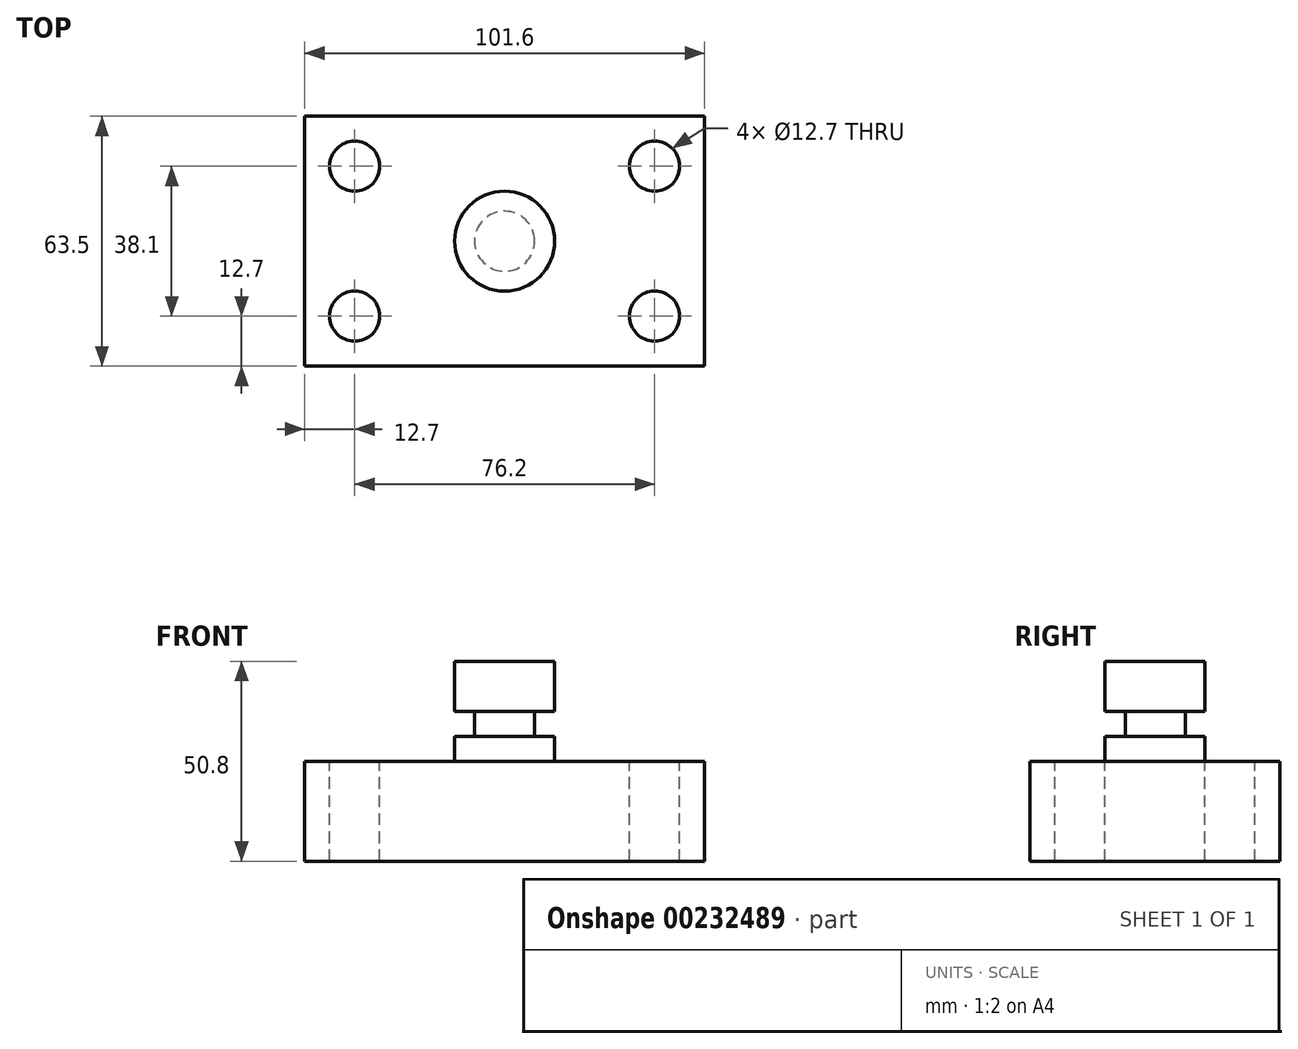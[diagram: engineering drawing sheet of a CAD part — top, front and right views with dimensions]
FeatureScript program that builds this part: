
annotation { "Feature Type Name" : "Feature", "Feature Type Description" : "" }
export const myFeature = defineFeature(function(context is Context, id is Id, definition is map)
    precondition{}
    {
        {
            var Q0;
            Q0=qCreatedBy(makeId("Top.planeOp"),FACE);
            var sketch = newSketch(context, id + "F0", { "sketchPlane" : qUnion([Q0])});
            skLineSegment(sketch, "E0.bottom", {"start": v(-50.8, 31.75) * mm, "end": v(50.8, 31.75) * mm});
            skLineSegment(sketch, "E0.top", {"start": v(-50.8, -31.75) * mm, "end": v(50.8, -31.75) * mm});
            skLineSegment(sketch, "E0.left", {"start": v(-50.8, 31.75) * mm, "end": v(-50.8, -31.75) * mm});
            skLineSegment(sketch, "E0.right", {"start": v(50.8, 31.75) * mm, "end": v(50.8, -31.75) * mm});
            skPoint(sketch, "E0.middle", {"position": v(0, 0) * mm});
            skSolve(sketch);
        }
        {
            var Q0;
            Q0 = qSketchRegion(id + "F0", true);
            extrude(context, id + "F1", {"entities" : qUnion([Q0]), "depth" : 25.4 * mm});
        }
        {
            var Q0;
            Q0=makeQuery(id+"F1.opExtrude","CAP_FACE",FACE,{"disambiguationData":[OSD([sQuery(id+"F0.wireOp",EDGE,"E0.bottom"),sQuery(id+"F0.wireOp",EDGE,"E0.top"),sQuery(id+"F0.wireOp",EDGE,"E0.left"),sQuery(id+"F0.wireOp",EDGE,"E0.right")])],"isStart":false});
            var sketch = newSketch(context, id + "F2", { "sketchPlane" : qUnion([Q0])});
            skCircle(sketch, "E1", {"center": v(38.1, 19.05) * mm, "radius": 6.35 * mm});
            skCircle(sketch, "E2", {"center": v(-38.1, 19.05) * mm, "radius": 6.35 * mm});
            skCircle(sketch, "E3", {"center": v(-38.1, -19.05) * mm, "radius": 6.35 * mm});
            skCircle(sketch, "E4", {"center": v(38.1, -19.05) * mm, "radius": 6.35 * mm});
            skSolve(sketch);
        }
        {
            var Q0;
            Q0=makeQuery(id+"F2.imprint","IMPRINT",FACE,{"disambiguationData":[TD([[makeQuery(id+"F2.imprint","IMPRINT",EDGE,{"derivedFrom":sQuery(id+"F2.wireOp",EDGE,"E1")}),1.0]])]});
            var Q1;
            Q1=makeQuery(id+"F2.imprint","IMPRINT",FACE,{"disambiguationData":[TD([[makeQuery(id+"F2.imprint","IMPRINT",EDGE,{"derivedFrom":sQuery(id+"F2.wireOp",EDGE,"E3")}),1.0]])]});
            var Q2;
            Q2=makeQuery(id+"F2.imprint","IMPRINT",FACE,{"disambiguationData":[TD([[makeQuery(id+"F2.imprint","IMPRINT",EDGE,{"derivedFrom":sQuery(id+"F2.wireOp",EDGE,"E4")}),1.0]])]});
            var Q3;
            Q3=makeQuery(id+"F2.imprint","IMPRINT",FACE,{"disambiguationData":[TD([[makeQuery(id+"F2.imprint","IMPRINT",EDGE,{"derivedFrom":sQuery(id+"F2.wireOp",EDGE,"E2")}),1.0]])]});
            extrude(context, id + "F3", {"entities" : qUnion([Q0, Q1, Q2, Q3]), "operationType" : NewBodyOperationType.REMOVE, "endBound" : BoundingType.THROUGH_ALL, "oppositeDirection" : true, "depth" : 24.38 * mm});
        }
        {
            var Q0;
            Q0=qCreatedBy(makeId("Front.planeOp"),FACE);
            var sketch = newSketch(context, id + "F4", { "sketchPlane" : qUnion([Q0])});
            skLineSegment(sketch, "E5.bottom", {"start": v(0, 50.8) * mm, "end": v(-12.7, 50.8) * mm});
            skLineSegment(sketch, "E5.top", {"start": v(0, 25.4) * mm, "end": v(-12.7, 25.4) * mm});
            skLineSegment(sketch, "E5.left", {"start": v(0, 50.8) * mm, "end": v(0, 25.4) * mm});
            skLineSegment(sketch, "E5.right", {"start": v(-12.7, 50.8) * mm, "end": v(-12.7, 25.4) * mm});
            skSolve(sketch);
        }
        {
            var Q0;
            Q0=makeQuery(id+"F4.imprint","IMPRINT",FACE,{"disambiguationData":[TD([[makeQuery(id+"F4.imprint","IMPRINT",EDGE,{"derivedFrom":sQuery(id+"F4.wireOp",EDGE,"E5.bottom")}),1.0]])]});
            var Q1;
            Q1=sQuery(id+"F4.wireOp",EDGE,"E5.left");
            revolve(context, id + "F5", {"operationType" : NewBodyOperationType.ADD, "entities" : qUnion([Q0]), "axis" : qUnion([Q1]), "revolveType" : RevolveType.FULL});
        }
        {
            var Q0;
            Q0=qCreatedBy(makeId("Front.planeOp"),FACE);
            var sketch = newSketch(context, id + "F6", { "sketchPlane" : qUnion([Q0])});
            skLineSegment(sketch, "E6.bottom", {"start": v(-34.2, 38.1) * mm, "end": v(-7.62, 38.1) * mm});
            skLineSegment(sketch, "E6.top", {"start": v(-34.2, 31.75) * mm, "end": v(-7.62, 31.75) * mm});
            skLineSegment(sketch, "E6.left", {"start": v(-34.2, 38.1) * mm, "end": v(-34.2, 31.75) * mm});
            skLineSegment(sketch, "E6.right", {"start": v(-7.62, 38.1) * mm, "end": v(-7.62, 31.75) * mm});
            skSolve(sketch);
        }
        {
            var Q0;
            Q0=makeQuery(id+"F6.imprint","IMPRINT",FACE,{"disambiguationData":[TD([[makeQuery(id+"F6.imprint","IMPRINT",EDGE,{"derivedFrom":sQuery(id+"F6.wireOp",EDGE,"E6.bottom")}),-1.0]])]});
            var Q1;
            Q1=makeQuery(id+"F5.opRevolve","SWEPT_EDGE",EDGE,{"disambiguationData":[OSD([sQuery(id+"F4.wireOp",EDGE,"E5.bottom"),sQuery(id+"F4.wireOp",EDGE,"E5.right")])]});
            revolve(context, id + "F7", {"operationType" : NewBodyOperationType.REMOVE, "entities" : qUnion([Q0]), "axis" : qUnion([Q1]), "revolveType" : RevolveType.FULL, "oppositeDirection" : true});
        }
    });
